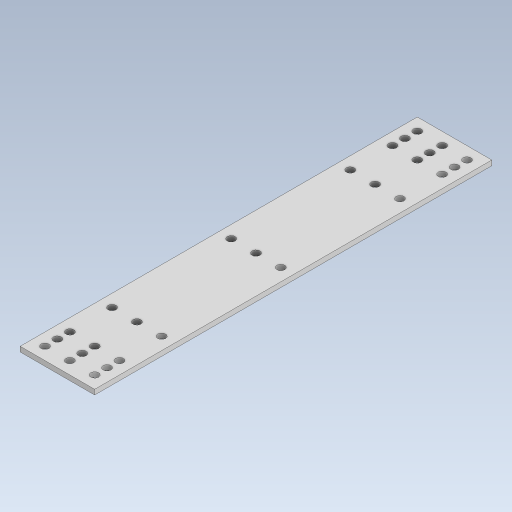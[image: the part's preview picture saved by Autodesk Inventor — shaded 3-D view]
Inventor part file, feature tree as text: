
AUTODESK INVENTOR PART (.ipt)
format: ipt  version: 2023.5 (Build 275446000, 446)  size: 146,944 bytes
history: native  units: mm
features: extrude x1, sketch x1
ambient origin geometry x8: Origin, YZ Plane, XZ Plane, XY Plane, X Axis, Y Axis, Z Axis, Center Point
bodies: Solid1 (feature_tree)
feature tree (2):
  extrude  "Extrusion1"  Depth=80.0mm
  sketch  "Sketch1"  dims[d0=30.0mm d1=80.0mm d2=3.2mm d3=5.0mm d4=5.0mm d5=3.2mm d6=3.2mm d7=3.2mm d8=5.0mm d9=3.2mm d10=3.2mm d11=3.2mm d12=5.0mm d13=3.2mm d14=3.2mm d15=3.2mm d17=3.2mm d18=3.2mm d19=2.0mm d20=0.0mm d21=3.2mm d22=48.0mm d23=3.2mm d24=3.2mm]
